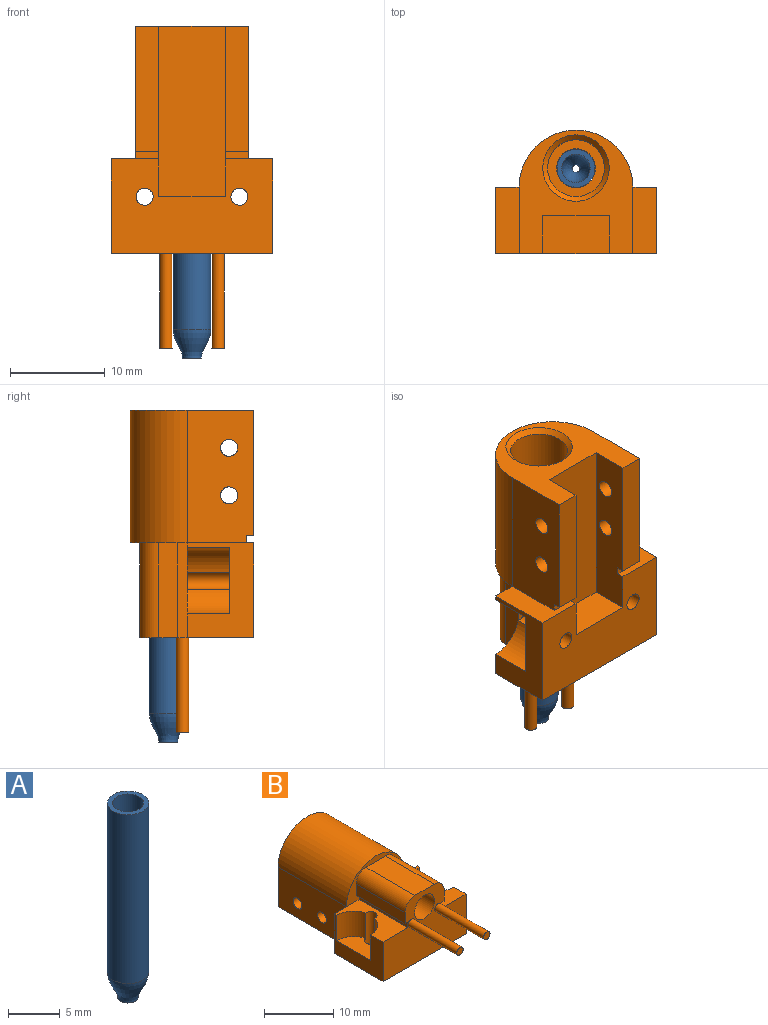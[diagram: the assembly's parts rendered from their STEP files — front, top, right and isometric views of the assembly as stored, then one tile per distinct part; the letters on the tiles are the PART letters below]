
ASSEMBLY  parts=2 mates=1
PART A: 6 faces, bbox 4x4x23 mm
  f0: revolved ~4x4mm, area 30.6mm2, adj f1,f5
  f1: plane 2x2mm, normal (0,0,-1), area 2.6mm2, adj f0,f2
  f2: revolved ~3x3mm, area 20mm2, adj f1,f3
  f3: cylinder r=1.5mm len=20mm, axis (0,0,-1), area 188.5mm2, adj f2,f4
  f4: plane 4x4mm, normal (0,0,1), area 5.5mm2, adj f3,f5
  f5: cylinder r=2mm len=20mm, axis (0,0,-1), area 251.3mm2, adj f0,f4
PART B: 52 faces, bbox 17x34x13 mm
  f0: plane 17x12mm, normal (0,-1,0), area 140.2mm2, adj f5,f6,f7,f8,f9,f10,f11,f12
  f1: plane 13.25x2.5mm, normal (0,0,-1), area 33.1mm2, adj f23,f26,f36,f46
  f2: plane 13.25x2.5mm, normal (0,0,-1), area 33.1mm2, adj f23,f24,f37,f45
  f3: plane 7x5mm, normal (0,1,0), area 19.4mm2, adj f5,f8,f12,f26,f36,f47
  f4: plane 7x5mm, normal (0,1,0), area 19.4mm2, adj f6,f8,f10,f24,f37,f44
  f5: plane 10x7mm, normal (-1,0,0), area 38.5mm2, adj f0,f3,f8,f12,f27,f28,f29
  f6: plane 10x7mm, normal (1,0,0), area 38.5mm2, adj f0,f4,f8,f10,f30,f31,f32
  f7: plane 10x4mm, normal (0,0,1), area 40mm2, adj f0,f14,f15,f22
  f8: plane 17x10mm, normal (0,0,-1), area 136.9mm2, adj f0,f3,f4,f5,f6,f20,f21,f36
  f9: plane 10x2mm, normal (1,0,0), area 20mm2, adj f0,f14,f19,f22
  f10: plane 10x5.1mm, normal (0,0,1), area 30.4mm2, adj f0,f4,f6,f18,f21,f22,f30,f31
  f11: plane 10x2mm, normal (-1,0,0), area 20mm2, adj f0,f15,f16,f22
  f12: plane 10x5.1mm, normal (0,0,1), area 30.4mm2, adj f0,f3,f5,f17,f20,f22,f27,f28
  f13: cylinder r=2.05mm len=12mm, axis (0,1,0), area 154.6mm2, adj f0,f34
  f14: cylinder r=2mm len=10mm, axis (0,1,0), area 31.4mm2, adj f0,f7,f9,f22
  f15: cylinder r=2mm len=10mm, axis (0,-1,0), area 31.4mm2, adj f0,f7,f11,f22
  f16: plane 10x0.6mm, normal (0,0,-1), area 6mm2, adj f0,f11,f17,f22
  f17: plane 10x1mm, normal (-1,0,0), area 10mm2, adj f0,f12,f16,f22
  f18: plane 10x1mm, normal (1,0,0), area 10mm2, adj f0,f10,f19,f22
  f19: plane 10x0.6mm, normal (0,0,-1), area 6mm2, adj f0,f9,f18,f22
  f20: cylinder r=0.9mm len=7mm, axis (0,0,-1), area 27.9mm2, adj f8,f12,f27,f28,f29
  f21: cylinder r=0.9mm len=7mm, axis (0,0,-1), area 27.9mm2, adj f8,f10,f30,f31,f32
  f22: plane 12x6mm, normal (0,-1,0), area 19.5mm2, adj f7,f9,f10,f11,f12,f14,f15,f16
  f23: plane 13x12mm, normal (0,1,0), area 74.1mm2, adj f1,f2,f24,f25,f26,f35,f36,f37
  f24: plane 14x7mm, normal (1,0,0), area 92.3mm2, adj f2,f4,f23,f25,f40,f42,f44,f45
  f25: cylinder r=6mm len=14mm, axis (0,-1,0), area 263.9mm2, adj f22,f23,f24,f26
  f26: plane 14x7mm, normal (-1,0,0), area 92.3mm2, adj f1,f3,f23,f25,f41,f43,f46,f47
  f27: cylinder r=3.5mm len=4.5mm, axis (0,0,1), area 20.7mm2, adj f5,f12,f20,f29
  f28: cylinder r=3.5mm len=4.5mm, axis (0,0,1), area 20.7mm2, adj f5,f12,f20,f29
  f29: plane 7x3.38mm, normal (0,0,1), area 18mm2, adj f5,f20,f27,f28
  f30: cylinder r=3.5mm len=4.5mm, axis (0,0,1), area 20.7mm2, adj f6,f10,f21,f32
  f31: cylinder r=3.5mm len=4.5mm, axis (0,0,1), area 20.7mm2, adj f6,f10,f21,f32
  f32: plane 7x3.38mm, normal (0,0,1), area 18mm2, adj f6,f21,f30,f31
  f33: cylinder r=3mm len=11.5mm, axis (0,1,0), area 216.8mm2, adj f34,f35
  f34: plane 6x6mm, normal (0,1,0), area 15.1mm2, adj f13,f33
  f35: cone r=3mm half-angle=45deg, axis (0,1,0), area 14.4mm2, adj f23,f33
  f36: plane 18x4mm, normal (1,0,0), area 66.3mm2, adj f1,f3,f8,f23,f38,f39,f41,f43
  f37: plane 18x4mm, normal (-1,0,0), area 66.3mm2, adj f2,f4,f8,f23,f38,f39,f40,f42
  f38: plane 18x7mm, normal (0,0,-1), area 126mm2, adj f23,f36,f37,f39
  f39: plane 7x4mm, normal (0,1,0), area 28mm2, adj f8,f36,f37,f38
  f40: cylinder r=0.9mm len=2.5mm, axis (1,0,0), area 14.1mm2, adj f24,f37
  f41: cylinder r=0.9mm len=2.5mm, axis (1,0,0), area 14.1mm2, adj f26,f36
  f42: cylinder r=0.9mm len=2.5mm, axis (1,0,0), area 14.1mm2, adj f24,f37
  f43: cylinder r=0.9mm len=2.5mm, axis (1,0,0), area 14.1mm2, adj f26,f36
  f44: plane 2.5x0.75mm, normal (0,0,-1), area 1.9mm2, adj f4,f24,f37,f45
  f45: plane 2.5x0.75mm, normal (0,-1,0), area 1.9mm2, adj f2,f24,f37,f44
  f46: plane 2.5x0.75mm, normal (0,-1,0), area 1.9mm2, adj f1,f26,f36,f47
  f47: plane 2.5x0.75mm, normal (0,0,-1), area 1.9mm2, adj f3,f26,f36,f46
  f48: cylinder r=0.65mm len=10mm, axis (0,1,0), area 40.8mm2, adj f0,f49
  f49: plane 1.3x1.3mm, normal (0,-1,0), area 1.3mm2, adj f48
  f50: cylinder r=0.65mm len=10mm, axis (0,1,0), area 40.8mm2, adj f0,f51
  f51: plane 1.3x1.3mm, normal (0,-1,0), area 1.3mm2, adj f50
PLACE A t=(8.5,9,-8)mm
PLACE B rot(axis=(0,0.71,0.71),180deg) t=(8.5,0,-22.41)mm fixed
MATE fastened A.f3 <-> B.f13  axis (0,0,1) through (8.5,9,12)mm
